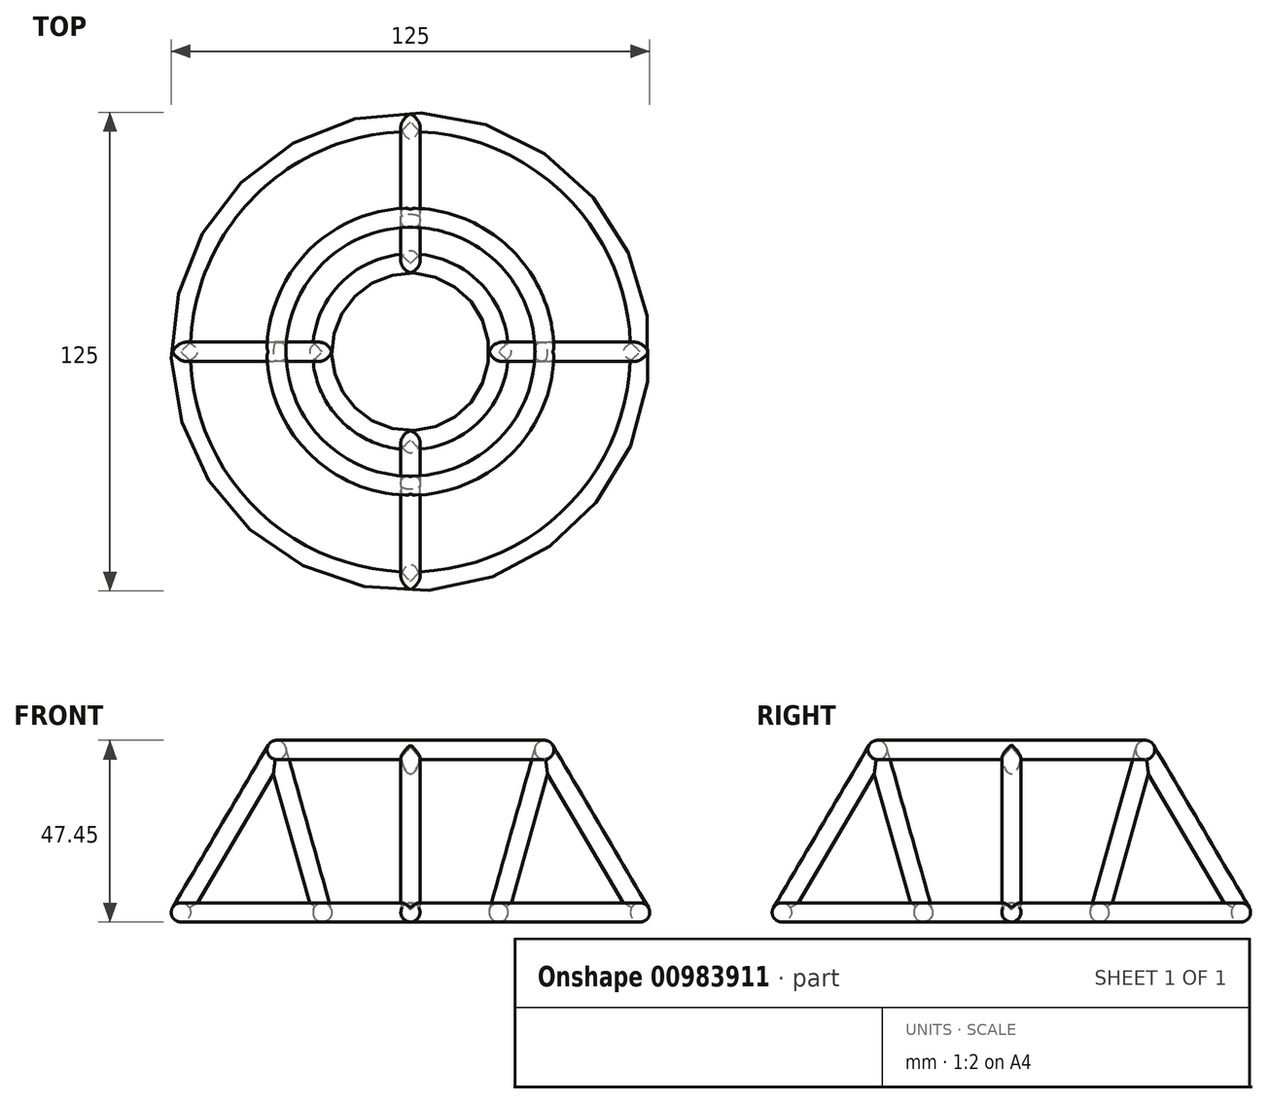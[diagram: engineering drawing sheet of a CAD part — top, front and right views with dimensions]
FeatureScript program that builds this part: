
annotation { "Feature Type Name" : "Feature", "Feature Type Description" : "" }
export const myFeature = defineFeature(function(context is Context, id is Id, definition is map)
    precondition{}
    {
        {
            var Q0;
            Q0=qCreatedBy(makeId("Front.planeOp"),FACE);
            var sketch = newSketch(context, id + "F0", { "sketchPlane" : qUnion([Q0])});
            skCircle(sketch, "E0", {"center": v(35, 42.45) * mm, "radius": 2.5 * mm});
            skCircle(sketch, "E1", {"center": v(60, 0) * mm, "radius": 2.5 * mm});
            skCircle(sketch, "E2", {"center": v(23.06, 0) * mm, "radius": 2.5 * mm});
            skLineSegment(sketch, "E3", {"start": v(0, 63.2) * mm, "end": v(0, 0) * mm, "construction": true});
            skSolve(sketch);
        }
        {
            var Q0;
            Q0=qCreatedBy(makeId("Front.planeOp"),FACE);
            var sketch = newSketch(context, id + "F1", { "sketchPlane" : qUnion([Q0])});
            skPoint(sketch, "E4.0", {"position": v(35, 42.45) * mm});
            skPoint(sketch, "E4.1", {"position": v(23.06, 0) * mm});
            skLineSegment(sketch, "E5", {"start": v(35, 42.45) * mm, "end": v(23.06, 0) * mm});
            skCircle(sketch, "E6.0", {"center": v(35, 42.45) * mm, "radius": 2.5 * mm, "construction": true});
            skCircle(sketch, "E6.1", {"center": v(23.06, 0) * mm, "radius": 2.5 * mm, "construction": true});
            skLineSegment(sketch, "E7", {"start": v(32.6, 43.13) * mm, "end": v(20.65, 0.68) * mm});
            skLineSegment(sketch, "E8", {"start": v(35, 42.45) * mm, "end": v(32.6, 43.13) * mm});
            skLineSegment(sketch, "E9", {"start": v(23.06, 0) * mm, "end": v(20.65, 0.68) * mm});
            skSolve(sketch);
        }
        {
            var Q0;
            Q0=makeQuery(id+"F1.imprint","IMPRINT",FACE,{"disambiguationData":[TD([[makeQuery(id+"F1.imprint","IMPRINT",EDGE,{"derivedFrom":sQuery(id+"F1.wireOp",EDGE,"E5")}),-1.0]])]});
            var Q1;
            Q1 = qConstructionFilter(qBodyType(qCreatedBy(id + "F1" ,EDGE), BodyType.WIRE), ConstructionObject.NO);
            var Q2;
            Q2=sQuery(id+"F1.wireOp",EDGE,"E5");
            revolve(context, id + "F2", {"surfaceOperationType" : NewSurfaceOperationType.ADD, "entities" : qUnion([Q0]), "surfaceEntities" : qUnion([Q1]), "axis" : qUnion([Q2]), "revolveType" : RevolveType.FULL});
        }
        {
            var Q0;
            Q0=qCreatedBy(makeId("Front.planeOp"),FACE);
            var sketch = newSketch(context, id + "F3", { "sketchPlane" : qUnion([Q0])});
            skCircle(sketch, "E10.0", {"center": v(23.06, 0) * mm, "radius": 2.5 * mm, "construction": true});
            skCircle(sketch, "E10.1", {"center": v(60, 0) * mm, "radius": 2.5 * mm, "construction": true});
            skPoint(sketch, "E10.2", {"position": v(60, 0) * mm});
            skPoint(sketch, "E10.3", {"position": v(23.06, 0) * mm});
            skLineSegment(sketch, "E11", {"start": v(60, 0) * mm, "end": v(23.06, 0) * mm});
            skLineSegment(sketch, "E12", {"start": v(23.06, 2.5) * mm, "end": v(60, 2.5) * mm});
            skLineSegment(sketch, "E13", {"start": v(60, 2.5) * mm, "end": v(60, 0) * mm});
            skLineSegment(sketch, "E14", {"start": v(23.06, 0) * mm, "end": v(23.06, 2.5) * mm});
            skSolve(sketch);
        }
        {
            var Q0;
            Q0 = qSketchRegion(id + "F3", true);
            var Q1;
            Q1=sQuery(id+"F3.wireOp",EDGE,"E11");
            revolve(context, id + "F4", {"operationType" : NewBodyOperationType.ADD, "surfaceOperationType" : NewSurfaceOperationType.NEW, "entities" : qUnion([Q0]), "axis" : qUnion([Q1]), "revolveType" : RevolveType.FULL});
        }
        {
            var Q0;
            Q0=qCreatedBy(makeId("Front.planeOp"),FACE);
            var sketch = newSketch(context, id + "F5", { "sketchPlane" : qUnion([Q0])});
            skCircle(sketch, "E15.0", {"center": v(35, 42.45) * mm, "radius": 2.5 * mm, "construction": true});
            skCircle(sketch, "E15.1", {"center": v(60, 0) * mm, "radius": 2.5 * mm, "construction": true});
            skPoint(sketch, "E15.2", {"position": v(35, 42.45) * mm});
            skPoint(sketch, "E15.3", {"position": v(60, 0) * mm});
            skLineSegment(sketch, "E16", {"start": v(35, 42.45) * mm, "end": v(60, 0) * mm});
            skLineSegment(sketch, "E17", {"start": v(60, 0) * mm, "end": v(62.15, 1.27) * mm});
            skLineSegment(sketch, "E18", {"start": v(62.15, 1.27) * mm, "end": v(37.15, 43.72) * mm});
            skLineSegment(sketch, "E19", {"start": v(37.15, 43.72) * mm, "end": v(35, 42.45) * mm});
            skSolve(sketch);
        }
        {
            var Q0;
            Q0 = qSketchRegion(id + "F5", true);
            var Q1;
            Q1=sQuery(id+"F5.wireOp",EDGE,"E16");
            revolve(context, id + "F6", {"operationType" : NewBodyOperationType.ADD, "surfaceOperationType" : NewSurfaceOperationType.NEW, "entities" : qUnion([Q0]), "axis" : qUnion([Q1]), "revolveType" : RevolveType.FULL});
        }
        {
            var Q0;
            Q0=makeQuery(id+"F2.opRevolve","SWEPT_BODY",BODY,{"disambiguationData":[OSD([sQuery(id+"F1.wireOp",EDGE,"E5"),sQuery(id+"F1.wireOp",EDGE,"E7"),sQuery(id+"F1.wireOp",EDGE,"E8"),sQuery(id+"F1.wireOp",EDGE,"E9")])]});
            var Q1;
            Q1=sQuery(id+"F0.wireOp",EDGE,"E3");
            circularPattern(context, id + "F7", {"operationType" : NewBodyOperationType.ADD, "entities" : qUnion([Q0]), "axis" : qUnion([Q1]), "angle" : 360 * degree, "instanceCount" : 4, "equalSpace" : true});
        }
        {
            var Q0;
            Q0 = qSketchRegion(id + "F0", true);
            var Q1;
            Q1=sQuery(id+"F0.wireOp",EDGE,"E3");
            revolve(context, id + "F8", {"operationType" : NewBodyOperationType.ADD, "surfaceOperationType" : NewSurfaceOperationType.NEW, "entities" : qUnion([Q0]), "axis" : qUnion([Q1]), "revolveType" : RevolveType.FULL});
        }
        {
            var Q0;
            Q0=qCreatedBy(makeId("Right.planeOp"),FACE);
            var Q1;
            Q1=sQuery(id+"F0.wireOp",VERTEX,"E2.center");
            cPlane(context, id + "F9", {"entities" : qUnion([Q0, Q1]), "cplaneType" : CPlaneType.PLANE_POINT, "offset" : 25 * mm, "width" : 150 * mm, "height" : 150 * mm});
        }
    });
